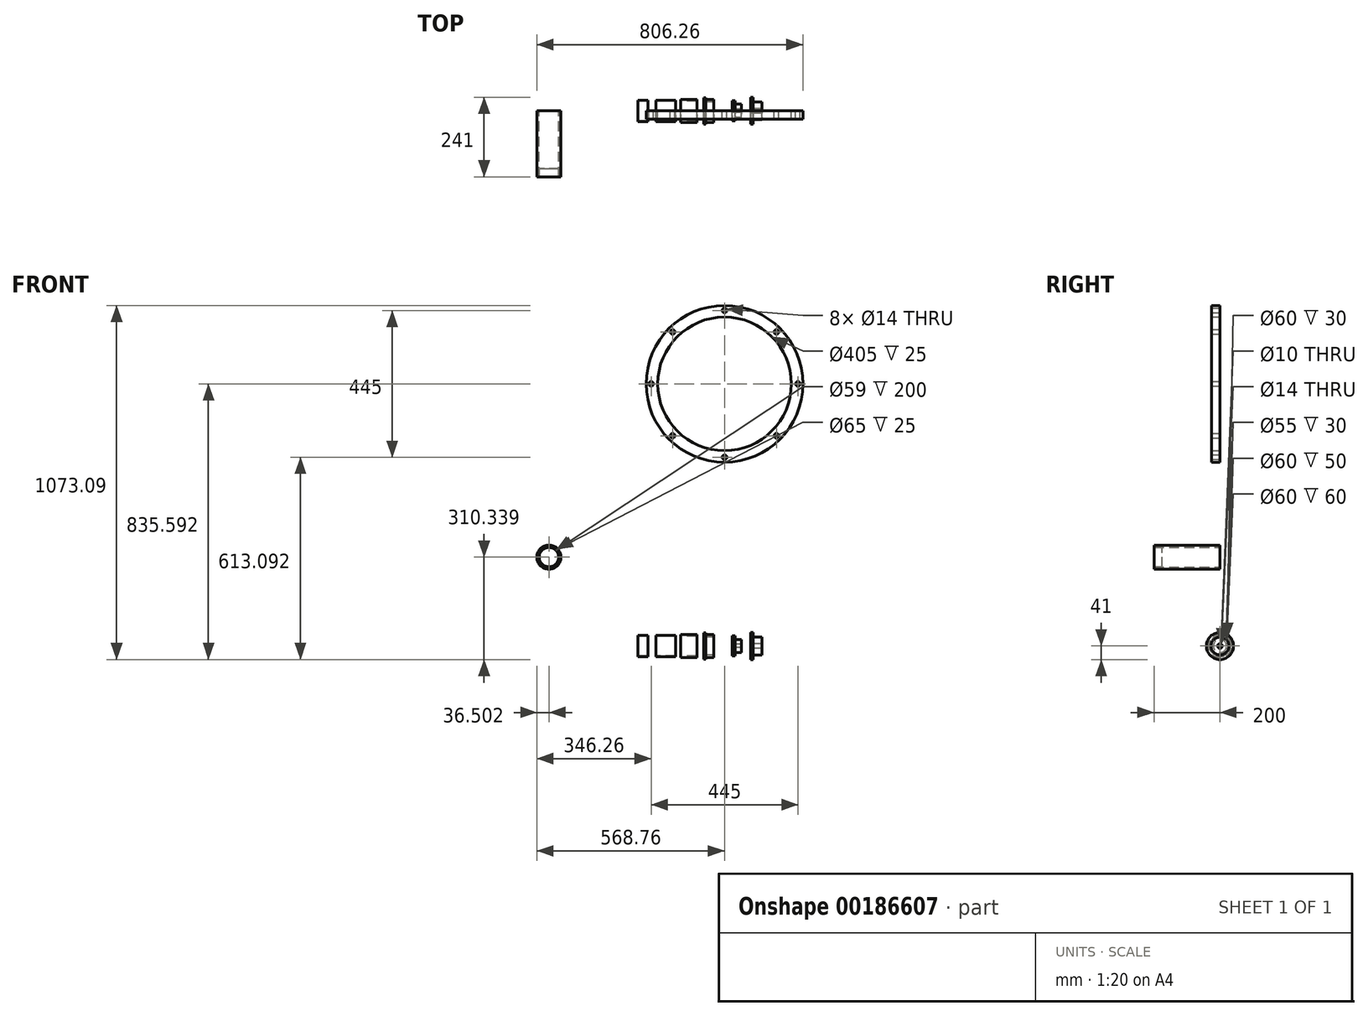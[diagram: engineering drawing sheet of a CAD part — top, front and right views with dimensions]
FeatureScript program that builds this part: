
annotation { "Feature Type Name" : "Feature", "Feature Type Description" : "" }
export const myFeature = defineFeature(function(context is Context, id is Id, definition is map)
    precondition{}
    {
        {
            var Q0;
            Q0=qCreatedBy(makeId("Front.planeOp"),FACE);
            var sketch = newSketch(context, id + "F0", { "sketchPlane" : qUnion([Q0])});
            skLineSegment(sketch, "E0", {"start": v(-116.72, 0) * mm, "end": v(106.12, 0) * mm, "construction": true});
            skLineSegment(sketch, "E1", {"start": v(-32.83, 27.5) * mm, "end": v(-62.83, 27.5) * mm});
            skLineSegment(sketch, "E2", {"start": v(-62.83, 27.5) * mm, "end": v(-62.83, 40) * mm});
            skLineSegment(sketch, "E3", {"start": v(-62.83, 40) * mm, "end": v(-56.83, 40) * mm});
            skLineSegment(sketch, "E4", {"start": v(-56.83, 40) * mm, "end": v(-56.83, 35) * mm});
            skLineSegment(sketch, "E5", {"start": v(-56.83, 35) * mm, "end": v(-32.83, 35) * mm});
            skLineSegment(sketch, "E6", {"start": v(-32.83, 35) * mm, "end": v(-32.83, 27.5) * mm});
            skSolve(sketch);
        }
        {
            var Q0;
            Q0 = qSketchRegion(id + "F0", true);
            var Q1;
            Q1=sQuery(id+"F0.wireOp",EDGE,"E0");
            revolve(context, id + "F1", {"entities" : qUnion([Q0]), "axis" : qUnion([Q1]), "revolveType" : RevolveType.FULL});
        }
        {
            var Q0;
            Q0=qCreatedBy(makeId("Front.planeOp"),FACE);
            var sketch = newSketch(context, id + "F2", { "sketchPlane" : qUnion([Q0])});
            skLineSegment(sketch, "E7.0", {"start": v(-116.72, 0) * mm, "end": v(106.12, 0) * mm, "construction": true});
            skLineSegment(sketch, "E8", {"start": v(23.58, 30.5) * mm, "end": v(23.58, 5) * mm});
            skLineSegment(sketch, "E9", {"start": v(23.58, 5) * mm, "end": v(51.58, 5) * mm});
            skLineSegment(sketch, "E10", {"start": v(51.58, 5) * mm, "end": v(51.58, 20) * mm});
            skLineSegment(sketch, "E11", {"start": v(51.58, 20) * mm, "end": v(31.58, 20) * mm});
            skLineSegment(sketch, "E12", {"start": v(31.58, 20) * mm, "end": v(31.58, 30.5) * mm});
            skLineSegment(sketch, "E13", {"start": v(31.58, 30.5) * mm, "end": v(23.58, 30.5) * mm});
            skLineSegment(sketch, "E14", {"start": v(78.45, 7) * mm, "end": v(113.45, 7) * mm});
            skLineSegment(sketch, "E15", {"start": v(113.45, 7) * mm, "end": v(113.45, 27) * mm});
            skLineSegment(sketch, "E16", {"start": v(113.45, 27) * mm, "end": v(86.45, 27) * mm});
            skLineSegment(sketch, "E17", {"start": v(86.45, 27) * mm, "end": v(86.45, 41) * mm});
            skLineSegment(sketch, "E18", {"start": v(86.45, 41) * mm, "end": v(78.45, 41) * mm});
            skLineSegment(sketch, "E19", {"start": v(78.45, 41) * mm, "end": v(78.45, 7) * mm});
            skSolve(sketch);
        }
        {
            var Q0;
            Q0 = qSketchRegion(id + "F2", true);
            var Q1;
            Q1=sQuery(id+"F2.wireOp",EDGE,"E7.0");
            revolve(context, id + "F3", {"entities" : qUnion([Q0]), "axis" : qUnion([Q1]), "revolveType" : RevolveType.FULL});
        }
        {
            var Q0;
            Q0=qCreatedBy(makeId("Front.planeOp"),FACE);
            var sketch = newSketch(context, id + "F4", { "sketchPlane" : qUnion([Q0])});
            skCircle(sketch, "E20", {"center": v(0, 794.6) * mm, "radius": 237.5 * mm});
            skCircle(sketch, "E21", {"center": v(0, 794.6) * mm, "radius": 202.5 * mm});
            skLineSegment(sketch, "E22", {"start": v(0, 1046.38) * mm, "end": v(0, 460.53) * mm, "construction": true});
            skCircle(sketch, "E23", {"center": v(0, 1017.1) * mm, "radius": 7 * mm});
            skCircle(sketch, "E24.1.0", {"center": v(-157.33, 951.92) * mm, "radius": 7 * mm});
            skCircle(sketch, "E24.2.0", {"center": v(-222.5, 794.6) * mm, "radius": 7 * mm});
            skCircle(sketch, "E24.3.0", {"center": v(-157.33, 637.26) * mm, "radius": 7 * mm});
            skCircle(sketch, "E24.4.0", {"center": v(0, 572.1) * mm, "radius": 7 * mm});
            skCircle(sketch, "E24.5.0", {"center": v(157.33, 637.26) * mm, "radius": 7 * mm});
            skCircle(sketch, "E24.6.0", {"center": v(222.5, 794.6) * mm, "radius": 7 * mm});
            skCircle(sketch, "E24.7.0", {"center": v(157.33, 951.92) * mm, "radius": 7 * mm});
            skSolve(sketch);
        }
        {
            var Q0;
            Q0 = qSketchRegion(id + "F4", true);
            extrude(context, id + "F5", {"entities" : qUnion([Q0]), "depth" : 25 * mm});
        }
        {
            var Q0;
            Q0=qCreatedBy(makeId("Front.planeOp"),FACE);
            var sketch = newSketch(context, id + "F6", { "sketchPlane" : qUnion([Q0])});
            skCircle(sketch, "E25", {"center": v(-532.26, 269.34) * mm, "radius": 36.5 * mm});
            skCircle(sketch, "E26.0", {"center": v(-532.26, 269.34) * mm, "radius": 29.5 * mm});
            skCircle(sketch, "E27", {"center": v(-532.26, 269.34) * mm, "radius": 30.15 * mm});
            skCircle(sketch, "E28.0", {"center": v(-532.26, 269.34) * mm, "radius": 25.15 * mm});
            skSolve(sketch);
        }
        {
            var Q0;
            Q0 = qSketchRegion(id + "F6", true);
            var Q1;
            Q1=makeQuery(id+"F6.imprint","IMPRINT",FACE,{"disambiguationData":[TD([[makeQuery(id+"F6.imprint","IMPRINT",EDGE,{"derivedFrom":sQuery(id+"F6.wireOp",EDGE,"E27")}),1.0]])]});
            extrude(context, id + "F7", {"entities" : qUnion([Q0, Q1]), "depth" : 200 * mm});
        }
        {
            var Q0;
            Q0=makeQuery(id+"F7.opExtrude","CAP_FACE",FACE,{"disambiguationData":[OSD([sQuery(id+"F6.wireOp",EDGE,"E25"),sQuery(id+"F6.wireOp",EDGE,"E26.0")])],"isStart":false});
            var sketch = newSketch(context, id + "F8", { "sketchPlane" : qUnion([Q0])});
            skCircle(sketch, "E29", {"center": v(-532.26, 269.34) * mm, "radius": 32.5 * mm});
            skCircle(sketch, "E30", {"center": v(-532.26, 269.34) * mm, "radius": 30 * mm});
            skSolve(sketch);
        }
        {
            var Q0;
            Q0 = qSketchRegion(id + "F8", true);
            extrude(context, id + "F9", {"entities" : qUnion([Q0]), "operationType" : NewBodyOperationType.REMOVE, "oppositeDirection" : true, "depth" : 25 * mm});
        }
        {
            var Q0;
            Q0=qCreatedBy(makeId("Front.planeOp"),FACE);
            var sketch = newSketch(context, id + "F10", { "sketchPlane" : qUnion([Q0])});
            skLineSegment(sketch, "E31.bottom", {"start": v(-133.38, 35) * mm, "end": v(-83.38, 35) * mm});
            skLineSegment(sketch, "E31.top", {"start": v(-133.38, 30) * mm, "end": v(-83.38, 30) * mm});
            skLineSegment(sketch, "E31.left", {"start": v(-133.38, 35) * mm, "end": v(-133.38, 30) * mm});
            skLineSegment(sketch, "E31.right", {"start": v(-83.38, 35) * mm, "end": v(-83.38, 30) * mm});
            skSolve(sketch);
        }
        {
            var Q0;
            Q0 = qSketchRegion(id + "F10", true);
            var Q1;
            Q1=sQuery(id+"F0.wireOp",EDGE,"E0");
            revolve(context, id + "F11", {"entities" : qUnion([Q0]), "axis" : qUnion([Q1]), "revolveType" : RevolveType.FULL});
        }
        {
            var Q0;
            Q0=qCreatedBy(makeId("Front.planeOp"),FACE);
            var sketch = newSketch(context, id + "F12", { "sketchPlane" : qUnion([Q0])});
            skLineSegment(sketch, "E32.bottom", {"start": v(-208.58, 32.5) * mm, "end": v(-148.58, 32.5) * mm});
            skLineSegment(sketch, "E32.top", {"start": v(-208.58, 30) * mm, "end": v(-148.58, 30) * mm});
            skLineSegment(sketch, "E32.left", {"start": v(-208.58, 32.5) * mm, "end": v(-208.58, 30) * mm});
            skLineSegment(sketch, "E32.right", {"start": v(-148.58, 32.5) * mm, "end": v(-148.58, 30) * mm});
            skLineSegment(sketch, "E33.bottom", {"start": v(-232.36, 30) * mm, "end": v(-262.36, 30) * mm});
            skLineSegment(sketch, "E33.top", {"start": v(-232.36, 32.5) * mm, "end": v(-262.36, 32.5) * mm});
            skLineSegment(sketch, "E33.left", {"start": v(-232.36, 30) * mm, "end": v(-232.36, 32.5) * mm});
            skLineSegment(sketch, "E33.right", {"start": v(-262.36, 30) * mm, "end": v(-262.36, 32.5) * mm});
            skSolve(sketch);
        }
        {
            var Q0;
            Q0 = qSketchRegion(id + "F12", true);
            var Q1;
            Q1=sQuery(id+"F0.wireOp",EDGE,"E0");
            revolve(context, id + "F13", {"entities" : qUnion([Q0]), "axis" : qUnion([Q1]), "revolveType" : RevolveType.FULL});
        }
    });
